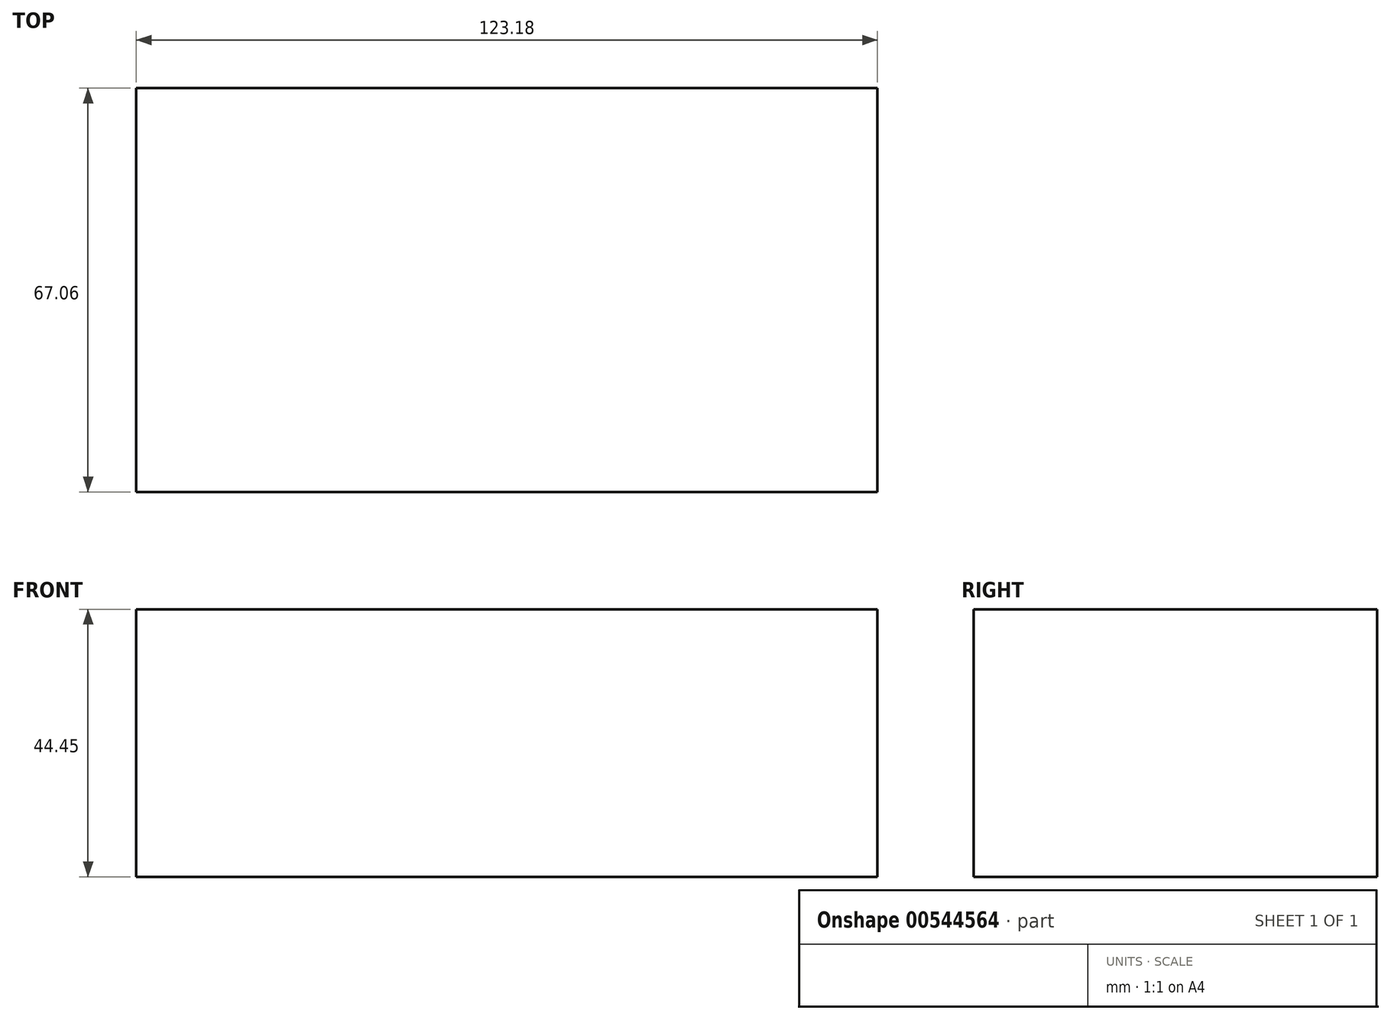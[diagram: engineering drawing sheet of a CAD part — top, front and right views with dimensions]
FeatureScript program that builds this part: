
annotation { "Feature Type Name" : "Feature", "Feature Type Description" : "" }
export const myFeature = defineFeature(function(context is Context, id is Id, definition is map)
    precondition{}
    {
        {
            var Q0;
            Q0=qCreatedBy(makeId("Top.planeOp"),FACE);
            var sketch = newSketch(context, id + "F0", { "sketchPlane" : qUnion([Q0])});
            skLineSegment(sketch, "E0", {"start": v(-114.83, 0) * mm, "end": v(8.35, 0) * mm});
            skLineSegment(sketch, "E1", {"start": v(8.35, 0) * mm, "end": v(8.35, 67.06) * mm});
            skLineSegment(sketch, "E2", {"start": v(-114.83, 0) * mm, "end": v(-114.83, 67.06) * mm});
            skLineSegment(sketch, "E3", {"start": v(-114.83, 67.06) * mm, "end": v(8.35, 67.06) * mm});
            skSolve(sketch);
        }
        {
            var Q0;
            Q0=sQuery(id+"F0.wireOp",EDGE,"E3");
            var Q1;
            Q1=sQuery(id+"F0.wireOp",EDGE,"E2");
            var Q2;
            Q2=sQuery(id+"F0.wireOp",EDGE,"E0");
            var Q3;
            Q3=sQuery(id+"F0.wireOp",EDGE,"E1");
            extrude(context, id + "F1", {"bodyType" : ToolBodyType.SURFACE, "surfaceEntities" : qUnion([Q0, Q1, Q2, Q3]), "depth" : 44.45 * mm, "offsetDistance" : 25.4 * mm});
        }
    });
